# Revit family: HydroTap_Dispenser_ZipUK_ClassicPlus
name_source: partatom
category: Plumbing Fixtures
revit_build: Autodesk Revit 2018 (Build: 20190510_1515(x64)
units: mm (PartAtom-declared; Revit-internal decimal feet)

## family parameters
Always vertical = No
Cut with Voids When Loaded = Yes
OmniClass Number = 23.31.11.00
OmniClass Title = Faucets
Part Type = Normal
Room Calculation Point = No
Round Connector Dimension = Use Diameter
Shared = No
Work Plane-Based = Yes

## types (1)
- Bright Chrome (91622, 91621, 91619)
    AssetType = Fixed
    CW Connection = Yes
    CodePerformance = UKCA and CE marked
    Color = Bright Chrome
    Default Elevation = 0 mm  [stored 0 ft]
    Description = HydroTap - Classic Plus Tap
    FixtureMaterial = Metal_BrightChrome_Zip
    Grade = Commercial
    HW Connection = Yes
    IfcExportAs = IfcValve
    IfcExportType = FAUCET
    Manufacturer = Zip Water UK
    ManufacturerOverallDepth = 151 mm
    ManufacturerOverallWidth = 46 mm  [stored 0.150919 ft]
    ManufacturerSpecCode = 91622, 91621, 91619
    ManufacturerURLProductSpecific = https://specify.zipwater.co.uk
    Model = Z00
    ModifiedIssue = 20210728 $
    Size = 46 x 151 x 215 mm
    SustainabilityPerformance = RoHS and WEEE compliant
    Type Comments = Bright Chrome Finish
    URL = https://www.zipwater.co.uk
    Uniclass2015Code = Pr_40_70_23_42
    Uniclass2015Title = Instant boiling and cold water taps
    Uniclass2015Version = Products v1.17
    Vent Connection = No
    Waste Connection = No

note: [stored X ft] marks values corroborated as IEEE doubles in the binary element streams (Revit-internal decimal feet)

## geometry (parser evidence)
native form markers: Sweep x5
no freeform markers — native parametric forms only
